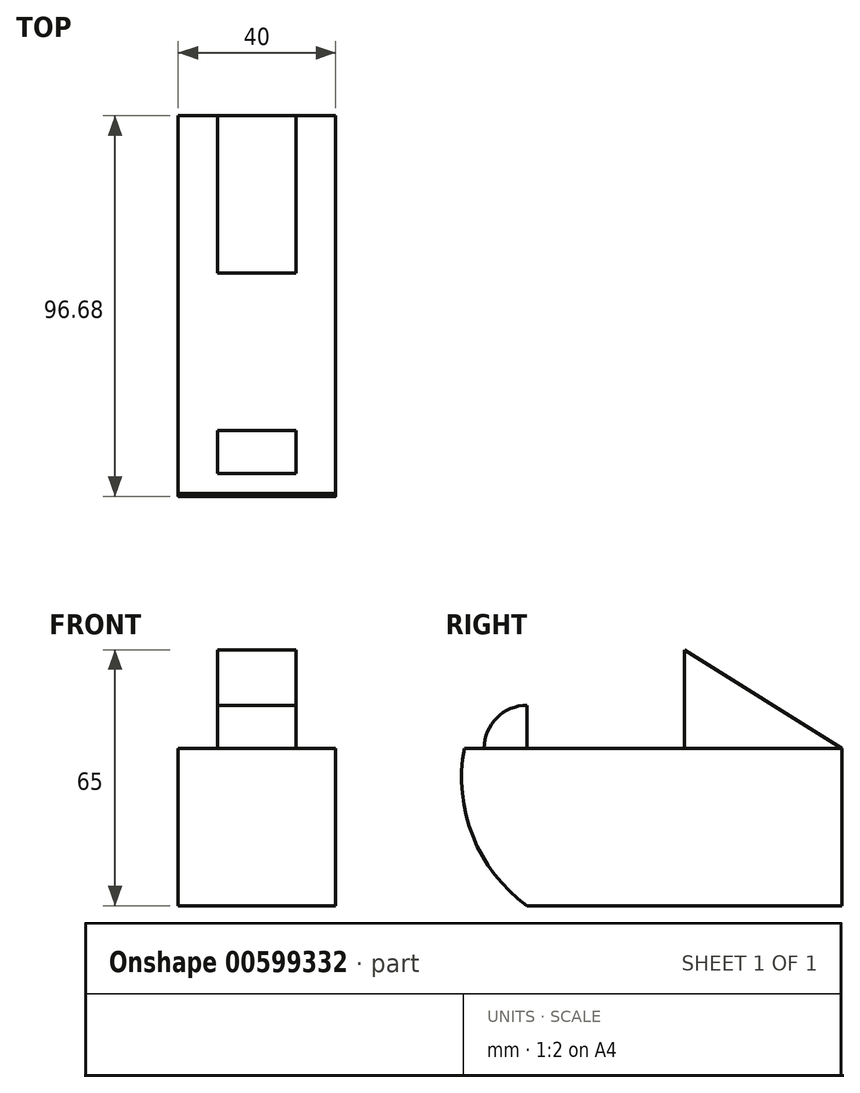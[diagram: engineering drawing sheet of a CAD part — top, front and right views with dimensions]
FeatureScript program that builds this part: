
annotation { "Feature Type Name" : "Feature", "Feature Type Description" : "" }
export const myFeature = defineFeature(function(context is Context, id is Id, definition is map)
    precondition{}
    {
        {
            var Q0;
            Q0=qCreatedBy(makeId("Right.planeOp"),FACE);
            var sketch = newSketch(context, id + "F0", { "sketchPlane" : qUnion([Q0])});
            skLineSegment(sketch, "E0.bottom", {"start": v(-40, 18.37) * mm, "end": v(40, 18.37) * mm});
            skLineSegment(sketch, "E0.top", {"start": v(-40, -21.63) * mm, "end": v(40, -21.63) * mm});
            skLineSegment(sketch, "E0.left", {"start": v(-40, 18.37) * mm, "end": v(-40, -21.63) * mm});
            skLineSegment(sketch, "E0.right", {"start": v(40, 18.37) * mm, "end": v(40, -21.63) * mm});
            skPoint(sketch, "E0.middle", {"position": v(0, -1.63) * mm});
            skLineSegment(sketch, "E1.bottom", {"start": v(-40, 18.37) * mm, "end": v(0, 18.37) * mm});
            skLineSegment(sketch, "E1.top", {"start": v(-40, 43.37) * mm, "end": v(0, 43.37) * mm});
            skLineSegment(sketch, "E1.left", {"start": v(-40, 18.37) * mm, "end": v(-40, 43.37) * mm});
            skLineSegment(sketch, "E1.right", {"start": v(0, 18.37) * mm, "end": v(0, 43.37) * mm});
            skLineSegment(sketch, "E2", {"start": v(0, 43.37) * mm, "end": v(40, 18.37) * mm});
            skArc(sketch, "E3", {"start": v(-40, 43.37) * mm, "mid": v(-56.68, 10.87) * mm, "end": v(-40, -21.63) * mm});
            skLineSegment(sketch, "E4", {"start": v(-40, 18.37) * mm, "end": v(-55.97, 18.37) * mm});
            skLineSegment(sketch, "E5", {"start": v(-40, 18.37) * mm, "end": v(-50.92, 18.37) * mm});
            skArc(sketch, "E6", {"start": v(-50.92, 18.37) * mm, "mid": v(-47.72, 26.1) * mm, "end": v(-40, 29.29) * mm});
            skLineSegment(sketch, "E7", {"start": v(-40, 18.37) * mm, "end": v(-40, 29.29) * mm});
            skLineSegment(sketch, "E8", {"start": v(-40, 29.29) * mm, "end": v(-27.5, 29.29) * mm});
            skLineSegment(sketch, "E9", {"start": v(-27.5, 29.29) * mm, "end": v(-27.5, 18.37) * mm});
            skLineSegment(sketch, "E10", {"start": v(-27.5, 18.37) * mm, "end": v(-17.5, 18.37) * mm});
            skLineSegment(sketch, "E11", {"start": v(-17.5, 18.37) * mm, "end": v(-17.5, 29.29) * mm});
            skLineSegment(sketch, "E12", {"start": v(-17.5, 29.29) * mm, "end": v(-27.5, 29.29) * mm});
            skLineSegment(sketch, "E13", {"start": v(-17.5, 29.29) * mm, "end": v(-5, 29.29) * mm});
            skLineSegment(sketch, "E14", {"start": v(-5, 29.29) * mm, "end": v(-5, 18.37) * mm});
            skLineSegment(sketch, "E15", {"start": v(-5, 18.37) * mm, "end": v(-17.5, 18.37) * mm});
            skLineSegment(sketch, "E16", {"start": v(11.15, 18.37) * mm, "end": v(-5, 18.37) * mm});
            skSolve(sketch);
        }
        {
            var Q0;
            Q0=makeQuery(id+"F0.imprint","IMPRINT",FACE,{"disambiguationData":[TD([[makeQuery(id+"F0.imprint","IMPRINT",EDGE,{"derivedFrom":sQuery(id+"F0.wireOp",EDGE,"E0.bottom")}),-1.0]])]});
            var Q1;
            {var subQ0=sQuery(id+"F0.wireOp",EDGE,"E0.left");Q1=makeQuery(id+"F0.imprint","IMPRINT",FACE,{"disambiguationData":[TD([[makeQuery(id+"F0.imprint","IMPRINT",EDGE,{"derivedFrom":subQ0}),-1.0]])]});}
            extrude(context, id + "F1", {"entities" : qUnion([Q0, Q1]), "endBound" : BoundingType.SYMMETRIC, "depth" : 40 * mm, "offsetDistance" : 25 * mm});
        }
        {
            var Q0;
            {var subQ0=sQuery(id+"F0.wireOp",EDGE,"E1.left");Q0=makeQuery(id+"F0.imprint","IMPRINT",FACE,{"disambiguationData":[TD([[makeQuery(id+"F0.imprint","IMPRINT",EDGE,{"derivedFrom":subQ0}),1.0]])]});}
            var Q1;
            Q1=makeQuery(id+"F0.imprint","IMPRINT",FACE,{"disambiguationData":[TD([[makeQuery(id+"F0.imprint","IMPRINT",EDGE,{"derivedFrom":sQuery(id+"F0.wireOp",EDGE,"E1.bottom")}),1.0]])]});
            extrude(context, id + "F2", {"entities" : qUnion([Q0, Q1]), "operationType" : NewBodyOperationType.ADD, "endBound" : BoundingType.SYMMETRIC, "depth" : 20 * mm, "offsetDistance" : 25 * mm});
        }
        {
            var Q0;
            Q0=makeQuery(id+"F0.imprint","IMPRINT",FACE,{"disambiguationData":[TD([[makeQuery(id+"F0.imprint","IMPRINT",EDGE,{"derivedFrom":sQuery(id+"F0.wireOp",EDGE,"E0.bottom")}),1.0]])]});
            extrude(context, id + "F3", {"entities" : qUnion([Q0]), "operationType" : NewBodyOperationType.ADD, "endBound" : BoundingType.SYMMETRIC, "depth" : 20 * mm, "offsetDistance" : 25 * mm});
        }
    });
